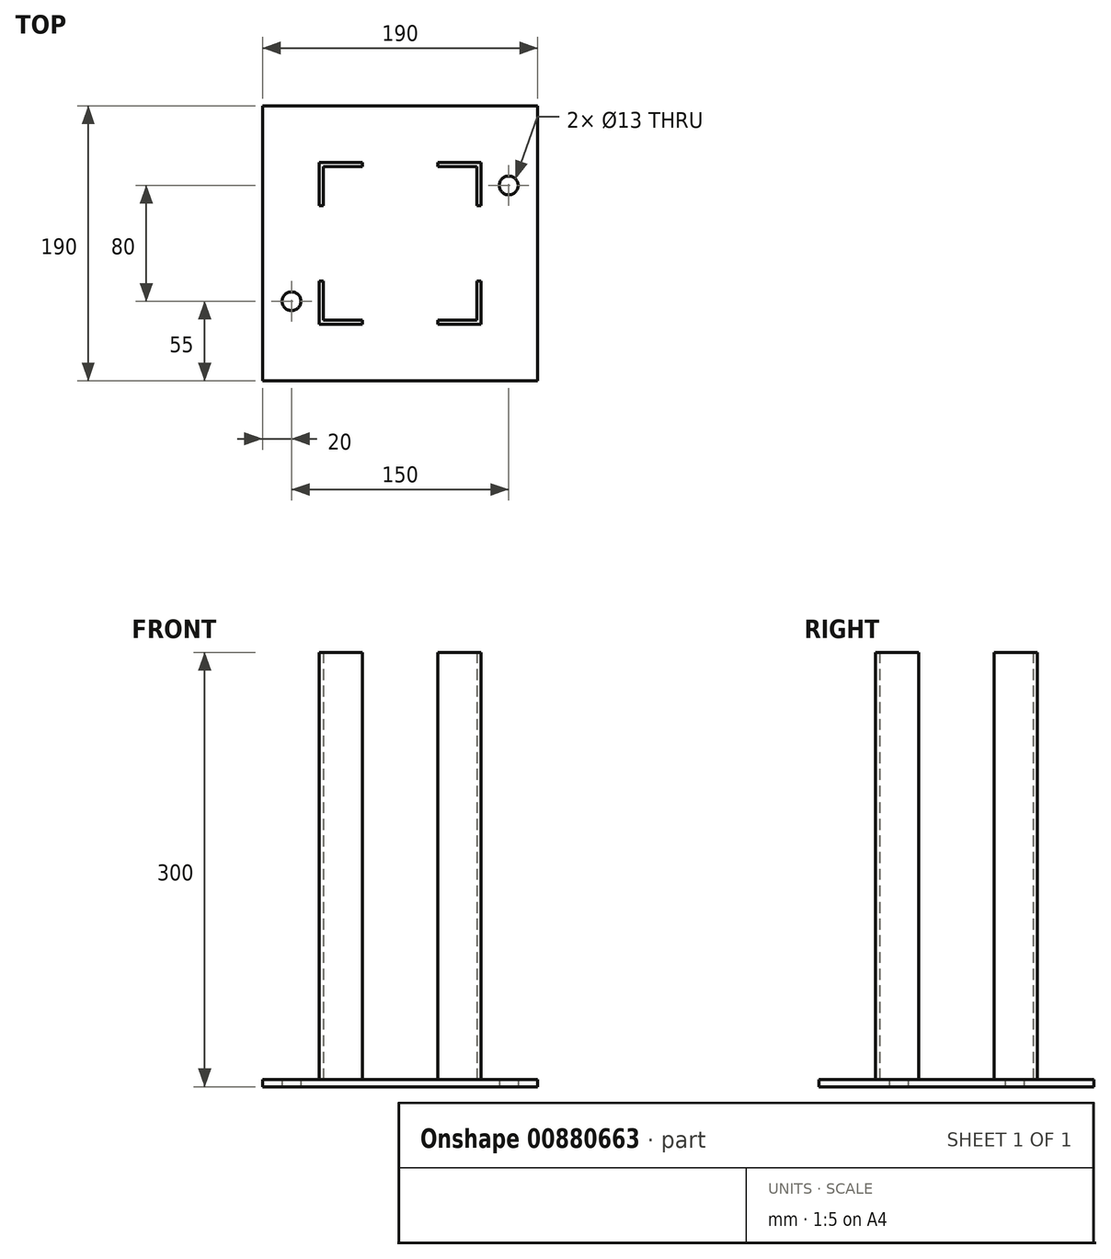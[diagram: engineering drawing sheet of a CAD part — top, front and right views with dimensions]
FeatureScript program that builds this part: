
annotation { "Feature Type Name" : "Feature", "Feature Type Description" : "" }
export const myFeature = defineFeature(function(context is Context, id is Id, definition is map)
    precondition{}
    {
        {
            var Q0;
            Q0=qCreatedBy(makeId("Top.planeOp"),FACE);
            var sketch = newSketch(context, id + "F0", { "sketchPlane" : qUnion([Q0])});
            skLineSegment(sketch, "E0.bottom", {"start": v(95, -95) * mm, "end": v(-95, -95) * mm});
            skLineSegment(sketch, "E0.top", {"start": v(95, 95) * mm, "end": v(-95, 95) * mm});
            skLineSegment(sketch, "E0.left", {"start": v(95, -95) * mm, "end": v(95, 95) * mm});
            skLineSegment(sketch, "E0.right", {"start": v(-95, -95) * mm, "end": v(-95, 95) * mm});
            skPoint(sketch, "E0.middle", {"position": v(0, 0) * mm});
            skLineSegment(sketch, "E1", {"start": v(-56, 56) * mm, "end": v(-56, 26) * mm});
            skLineSegment(sketch, "E2", {"start": v(-56, 56) * mm, "end": v(-26, 56) * mm});
            skLineSegment(sketch, "E3", {"start": v(26, 56) * mm, "end": v(56, 56) * mm});
            skLineSegment(sketch, "E4", {"start": v(56, 56) * mm, "end": v(56, 26) * mm});
            skLineSegment(sketch, "E5", {"start": v(56, -26) * mm, "end": v(56, -56) * mm});
            skLineSegment(sketch, "E6", {"start": v(56, -56) * mm, "end": v(26, -56) * mm});
            skLineSegment(sketch, "E7", {"start": v(-56, -26) * mm, "end": v(-56, -56) * mm});
            skLineSegment(sketch, "E8", {"start": v(-56, -56) * mm, "end": v(-26, -56) * mm});
            skLineSegment(sketch, "E9.0", {"start": v(-53, -53) * mm, "end": v(-26, -53) * mm});
            skLineSegment(sketch, "E9.1", {"start": v(-53, -26) * mm, "end": v(-53, -53) * mm});
            skLineSegment(sketch, "E10", {"start": v(-56, -26) * mm, "end": v(-53, -26) * mm});
            skLineSegment(sketch, "E11", {"start": v(-26, -53) * mm, "end": v(-26, -56) * mm});
            skLineSegment(sketch, "E12.0", {"start": v(53, -53) * mm, "end": v(26, -53) * mm});
            skLineSegment(sketch, "E12.1", {"start": v(53, -26) * mm, "end": v(53, -53) * mm});
            skLineSegment(sketch, "E13.0", {"start": v(53, 53) * mm, "end": v(53, 26) * mm});
            skLineSegment(sketch, "E13.1", {"start": v(26, 53) * mm, "end": v(53, 53) * mm});
            skLineSegment(sketch, "E14.0", {"start": v(-53, 53) * mm, "end": v(-26, 53) * mm});
            skLineSegment(sketch, "E14.1", {"start": v(-53, 53) * mm, "end": v(-53, 26) * mm});
            skLineSegment(sketch, "E15", {"start": v(53, -26) * mm, "end": v(56, -26) * mm});
            skLineSegment(sketch, "E16", {"start": v(26, -53) * mm, "end": v(26, -56) * mm});
            skLineSegment(sketch, "E17", {"start": v(56, 26) * mm, "end": v(53, 26) * mm});
            skLineSegment(sketch, "E18", {"start": v(26, 56) * mm, "end": v(26, 53) * mm});
            skLineSegment(sketch, "E19", {"start": v(-26, 56) * mm, "end": v(-26, 53) * mm});
            skLineSegment(sketch, "E20", {"start": v(-56, 26) * mm, "end": v(-53, 26) * mm});
            skCircle(sketch, "E21", {"center": v(-75, -40) * mm, "radius": 6.5 * mm});
            skCircle(sketch, "E22", {"center": v(75, 40) * mm, "radius": 6.5 * mm});
            skSolve(sketch);
        }
        {
            var Q0;
            Q0=makeQuery(id+"F0.imprint","IMPRINT",FACE,{"disambiguationData":[TD([[makeQuery(id+"F0.imprint","IMPRINT",EDGE,{"derivedFrom":sQuery(id+"F0.wireOp",EDGE,"E0.bottom")}),-1.0]])]});
            extrude(context, id + "F1", {"entities" : qUnion([Q0]), "depth" : 5 * mm, "offsetDistance" : 25 * mm});
        }
        {
            var Q0;
            Q0=makeQuery(id+"F0.imprint","IMPRINT",FACE,{"disambiguationData":[TD([[makeQuery(id+"F0.imprint","IMPRINT",EDGE,{"derivedFrom":sQuery(id+"F0.wireOp",EDGE,"E7")}),1.0]])]});
            var Q1;
            Q1=makeQuery(id+"F0.imprint","IMPRINT",FACE,{"disambiguationData":[TD([[makeQuery(id+"F0.imprint","IMPRINT",EDGE,{"derivedFrom":sQuery(id+"F0.wireOp",EDGE,"E5")}),-1.0]])]});
            var Q2;
            Q2=makeQuery(id+"F0.imprint","IMPRINT",FACE,{"disambiguationData":[TD([[makeQuery(id+"F0.imprint","IMPRINT",EDGE,{"derivedFrom":sQuery(id+"F0.wireOp",EDGE,"E3")}),-1.0]])]});
            var Q3;
            Q3=makeQuery(id+"F0.imprint","IMPRINT",FACE,{"disambiguationData":[TD([[makeQuery(id+"F0.imprint","IMPRINT",EDGE,{"derivedFrom":sQuery(id+"F0.wireOp",EDGE,"E1")}),1.0]])]});
            extrude(context, id + "F2", {"entities" : qUnion([Q0, Q1, Q2, Q3]), "operationType" : NewBodyOperationType.ADD, "depth" : 300 * mm, "offsetDistance" : 25 * mm});
        }
    });
